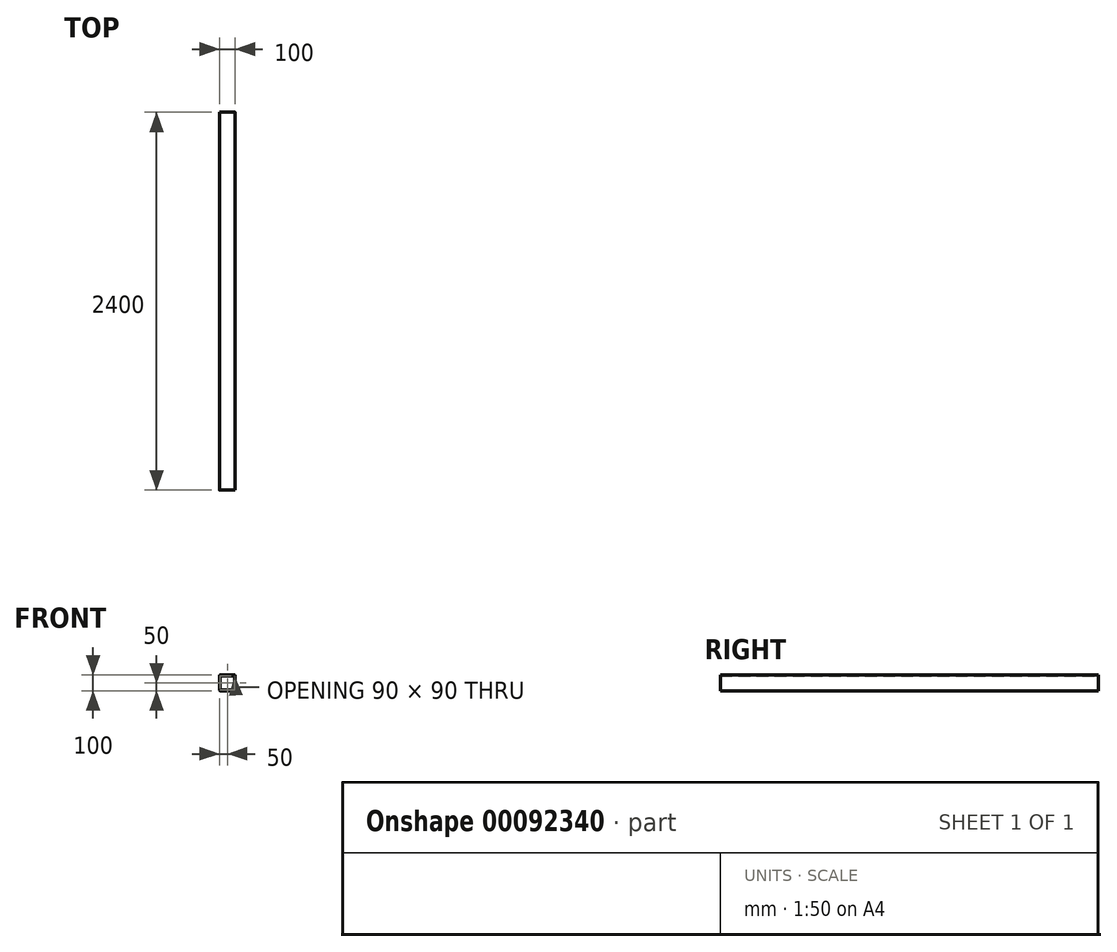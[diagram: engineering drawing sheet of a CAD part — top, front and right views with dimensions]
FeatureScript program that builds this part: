
annotation { "Feature Type Name" : "Feature", "Feature Type Description" : "" }
export const myFeature = defineFeature(function(context is Context, id is Id, definition is map)
    precondition{}
    {
        {
            var Q0;
            Q0=qCreatedBy(makeId("Front.planeOp"),FACE);
            var sketch = newSketch(context, id + "F0", { "sketchPlane" : qUnion([Q0])});
            skLineSegment(sketch, "E0.bottom", {"start": v(5, 0) * mm, "end": v(95, 0) * mm});
            skLineSegment(sketch, "E0.top", {"start": v(5, 100) * mm, "end": v(95, 100) * mm});
            skLineSegment(sketch, "E0.left", {"start": v(0, 5) * mm, "end": v(0, 95) * mm});
            skLineSegment(sketch, "E0.right", {"start": v(100, 5) * mm, "end": v(100, 95) * mm});
            skPoint(sketch, "E1.visualSharp", {"position": v(0, 100) * mm});
            skArc(sketch, "E1.filletArc", {"start": v(5, 100) * mm, "mid": v(1.46, 98.54) * mm, "end": v(0, 95) * mm});
            skPoint(sketch, "E2.visualSharp", {"position": v(100, 100) * mm});
            skArc(sketch, "E2.filletArc", {"start": v(100, 95) * mm, "mid": v(98.54, 98.54) * mm, "end": v(95, 100) * mm});
            skPoint(sketch, "E3.visualSharp", {"position": v(100, 0) * mm});
            skArc(sketch, "E3.filletArc", {"start": v(95, 0) * mm, "mid": v(98.54, 1.46) * mm, "end": v(100, 5) * mm});
            skPoint(sketch, "E4.visualSharp", {"position": v(0, 0) * mm});
            skArc(sketch, "E4.filletArc", {"start": v(0, 5) * mm, "mid": v(1.46, 1.46) * mm, "end": v(5, 0) * mm});
            skLineSegment(sketch, "E5.0", {"start": v(10, 95) * mm, "end": v(90, 95) * mm});
            skLineSegment(sketch, "E6.0", {"start": v(95, 10) * mm, "end": v(95, 90) * mm});
            skLineSegment(sketch, "E7.0", {"start": v(10, 5) * mm, "end": v(90, 5) * mm});
            skLineSegment(sketch, "E8.0", {"start": v(5, 10) * mm, "end": v(5, 90) * mm});
            skArc(sketch, "E9.filletArc", {"start": v(10, 95) * mm, "mid": v(6.46, 93.54) * mm, "end": v(5, 90) * mm});
            skArc(sketch, "E10.filletArc", {"start": v(5, 10) * mm, "mid": v(6.46, 6.46) * mm, "end": v(10, 5) * mm});
            skArc(sketch, "E11.filletArc", {"start": v(90, 5) * mm, "mid": v(93.54, 6.46) * mm, "end": v(95, 10) * mm});
            skArc(sketch, "E12.filletArc", {"start": v(95, 90) * mm, "mid": v(93.54, 93.54) * mm, "end": v(90, 95) * mm});
            skSolve(sketch);
        }
        {
            var Q0;
            Q0=qSketchRegion(id+"F0",true);
            extrude(context, id + "F1", {"entities" : qUnion([Q0]), "depth" : 2400 * mm, "offsetDistance" : 25 * mm});
        }
    });
